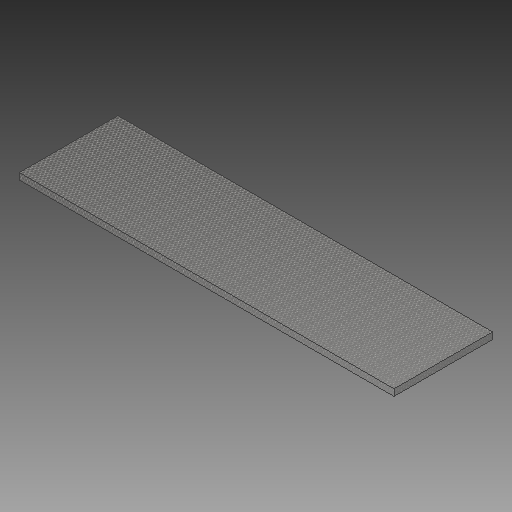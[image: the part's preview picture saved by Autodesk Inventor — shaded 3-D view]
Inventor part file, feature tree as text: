
AUTODESK INVENTOR PART (.ipt)
format: ipt  version: 2019 (Build 230136000, 136)  size: 150,528 bytes
history: native  units: mm
features: extrude x1, sketch x1
ambient origin geometry x8: Origin, YZ Plane, XZ Plane, XY Plane, X Axis, Y Axis, Z Axis, Center Point
bodies: Solid1 (feature_tree)
feature tree (2):
  extrude  "Extrusion1"  Depth=10.0mm
  sketch  "Sketch1"  dims[d0=570.0mm d1=10.0mm d2=150.0mm d3=0.0mm]
